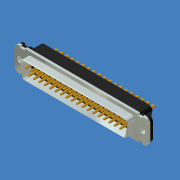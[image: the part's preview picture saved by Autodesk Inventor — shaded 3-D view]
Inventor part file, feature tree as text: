
AUTODESK INVENTOR PART (.ipt)
format: ipt  version: 2019 (Build 230136000, 136)  size: 491,520 bytes
history: native  units: mm (DEFAULTED — no unit token found)
features: extrude x12, pattern_linear x6, sketch x4, fillet x4, chamfer x1
ambient origin geometry x8: Origin, YZ Plane, XZ Plane, XY Plane, X Axis, Y Axis, Z Axis, Center Point
bodies: Solid1 (feature_tree)
feature tree (27):
  sketch  "Sketch1"  dims[d0=1.745329mm d6=0.381mm d7=2.418418mm d8=0.855895mm d9=2.418418mm]
  extrude  "Extrusion1"  Depth=0.381mm
  extrude  "Extrusion2"  Depth=1.314425mm
  fillet  "Fillet4"  Radius=1.397mm
  extrude  "Pin1"  Depth=5.08mm TaperAngle=0.0deg
  extrude  "Pin2"  Depth=5.08mm TaperAngle=0.0deg
  extrude  "Pin50"  Depth=10.8966mm
  fillet  "Fillet1"  Radius=2.794mm
  fillet  "Fillet2"  Radius=180.0mm
  fillet  "Fillet50"  Radius=2.794mm
  extrude  "Extrusion5"  Depth=1.909443mm
  extrude  "Extrusion6"  Depth=0.254mm
  sketch  "Sketch4"  dims[d24=5.08mm d25=0.0mm d26=5.08mm d27=0.0mm d28=190.0mm d30=2.794mm d31=180.0mm d33=2.794mm d34=1.909443mm d35=0.254mm d36=1.6002mm d37=0.0mm d38=5.08mm d39=0.0mm d44=0.4953mm d45=0.4953mm d46=1.016mm d52=2.8448mm d53=5.08mm d54=0.0mm d55=0.4953mm d56=5.08mm d57=0.0mm d58=0.2032mm d59=0.2032mm d60=190.0mm d62=2.794mm d63=0.381mm d67=5.1054mm d68=0.0mm d69=5.6388mm d70=0.0mm d71=5.6388mm d72=0.0mm d73=5.6388mm d74=0.0mm d75=190.0mm d77=2.794mm d78=180.0mm d80=2.794mm d81=190.0mm d83=2.794mm d86=1.909443mm d87=10.8966mm d88=57.9628mm d91=45.0deg]
  extrude  "ExtrudeSgr50"  Depth=1.6002mm TaperAngle=0.0deg
  chamfer  "Chamfer50"  Distance=5.08mm
  pattern_linear  "Pattern1"  Spacing1=0.4953mm  [1 undecoded]
  pattern_linear  "Pattern2"  Spacing1=0.4953mm  [1 undecoded]
  pattern_linear  "Pattern50"  Spacing1=1.016mm  [1 undecoded]
  extrude  "Female"  Depth=10.8966mm
  extrude  "Socket1"  Depth=5.08mm
  extrude  "Socket2"  TaperAngle=0.0deg  [1 undecoded]
  extrude  "Socket50"  Depth=0.4953mm
  pattern_linear  "Pattern5"  Spacing1=5.08mm  [1 undecoded]
  pattern_linear  "Pattern6"  Spacing1=0.0mm  [1 undecoded]
  pattern_linear  "Pattern7"  Spacing1=0.2032mm  [1 undecoded]
  sketch  "Sketch2"  dims[d11=1.314425mm d15=2.54mm d19=1.397mm]
  sketch  "Sketch3"  dims[d20=1.27mm d21=0.0mm d22=5.08mm d23=0.0mm]
note: 7 required parameter values undecoded (feature->parameter linkage not recoverable at this tier; creation-order binding heuristic only, values carry confidence <= 0.55)
